# Revit family: Deca_Tanque 40 Litros_Tanque Medio_TQ.03
name_source: partatom
category: Plumbing Fixtures
units: mm (PartAtom-declared; Revit-internal decimal feet)

## family parameters
Cut with Voids When Loaded = No
Host = Face
Part Type = Normal
Room Calculation Point = No
Round Connector Dimension = Use Radius
Shared = Yes

## types (1)
- TQ.03.17_Branco
    Acompanha o Produto = -
    Aprovado por = quattroD
    Atendimento ao Cliente = 0800-0117073
    Categoria = TANQUES
    Composição Anel Vedação = -
    Composição Assento = -
    Composição Básica = Argila, feldspato, caulim, vidrados e corantes inorgânicos.
    Composição Componente = Não Possui
    Consumo = -
    Cor Interna = -
    Cor Principal = Branco
    Cor Secundária = -
    Cores Componente = Não Possui
    Criado por = quattroD
    Código Pai = TQ.03
    Default Elevation = 0 m
    Description = Tanque 40 litros
    Diâmetro Ponto de Esgoto = 0.03 m
    Informações Complementares = -
    Itens de Instalação = 1606.C.DUO; 1680.C.114; 1682.C.112; CT.25.17; FT.11.01
    Linha = Tanque Medio
    Manufacturer = Deca
    Material = Deca_Branco
    Model = TQ.03.17
    Norma = NBR-16728-1;NBR-16728-2
    Peso Líquido (Kg) = 27.943
    Pressão máx. funcionamento = -
    Pressão mín. Aquec. Acúmulo = -
    Pressão mín. Aquec. Passagem = -
    Pressão mín. funcionamento = -
    Raio Ponto de Esgoto = 0.01 m
    Saída de Esgoto = -
    Segmento = Banheiro Médio
    Tipo de dispositivo economizador = -
    Tipo de mecanismo utilizado = -
    Tipo de rosca de entrada = -
    Tipo de rosca de saída = -
    URL = www.deca.com.br
    Vazão na Pressão máx. (L/min) = -
    Vazão na Pressão mín. (L/min) = -
    WFU = 0

## geometry (parser evidence)
native form markers: Sweep x4
no freeform markers — native parametric forms only
